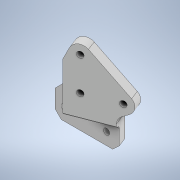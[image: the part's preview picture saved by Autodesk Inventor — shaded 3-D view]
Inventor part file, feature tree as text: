
AUTODESK INVENTOR PART (.ipt)
format: ipt  version: 2023 (Build 270158000, 158)  size: 296,448 bytes
history: native  units: mm
features: reference x11, extrude x9, sketch x9, projected_geometry x8, other x7, fillet x6, chamfer x4, thicken_offset x2
ambient origin geometry x8: Origin, YZ Plane, XZ Plane, XY Plane, X Axis, Y Axis, Z Axis, Center Point
bodies: Solid1 (feature_tree)
feature tree (56):
  extrude  "Extrusion1"  Depth=20.0mm
  extrude  "Extrusion2"  Depth=2.0mm
  extrude  "Extrusion3"  Depth=3.0mm TaperAngle=0.0deg
  extrude  "Extrusion4"  Depth=3.0mm TaperAngle=0.0deg
  extrude  "Extrusion5"  Depth=6.0mm
  extrude  "Extrusion6"  Depth=3.0mm
  extrude  "Extrusion7"  Depth=3.0mm TaperAngle=0.0deg
  fillet  "Fillet1"  Radius=6.0mm
  fillet  "Fillet2"  Radius=120.0mm
  chamfer  "Chamfer1"  Distance=3.0mm Angle=45.0deg
  extrude  "Extrusion8"  Depth=2.0mm
  extrude  "Extrusion9"  Depth=2.0mm
  chamfer  "Chamfer3"  Distance=2.0mm
  chamfer  "Chamfer4"  Distance=120.0mm
  thicken_offset  "Thicken1"
  thicken_offset  "Thicken2"
  fillet  "Fillet6"  Radius=120.0mm
  fillet  "Fillet7"  Radius=2.0mm
  fillet  "Fillet8"  Radius=2.0mm
  chamfer  "Chamfer5"  Distance=2.0mm
  fillet  "Fillet10"  Radius=1.5mm
  sketch  "Sketch1"  dims[d0=8.0mm d1=20.0mm]
  reference  "Reference1"
  reference  "Reference2"
  reference  "Reference3"
  sketch  "Sketch2"  dims[d2=2.0mm d3=2.0mm]
  projected_geometry  "Projected Loop1"
  reference  "Reference4"
  sketch  "Sketch3"  dims[d4=3.0mm d5=0.0mm d6=20.0mm d7=0.0mm]
  projected_geometry  "Projected Loop2"
  projected_geometry  "Projected Loop3"
  sketch  "Sketch4"  dims[d8=3.0mm d9=0.0mm d10=3.0mm d11=0.0mm]
  projected_geometry  "Projected Loop4"
  sketch  "Sketch5"  dims[d12=6.0mm d13=6.0mm]
  reference  "Reference5"
  reference  "Reference6"
  projected_geometry  "Projected Loop5"
  sketch  "Sketch6"  dims[d14=3.0mm d15=0.0mm d16=6.0mm]
  reference  "Reference7"
  reference  "Reference8"
  projected_geometry  "Projected Loop6"
  sketch  "Sketch7"  dims[d17=6.0mm d18=3.0mm d19=0.0mm d20=6.0mm d21=120.0mm d22=0.0mm]
  projected_geometry  "Projected Loop7"
  sketch  "Sketch8"  dims[d23=3.0mm]
  reference  "Reference9"
  reference  "Reference10"
  reference  "Reference11"
  sketch  "Sketch9"  dims[d24=1.0mm d25=3.0mm d26=2.0mm d27=45.0deg d28=2.0mm d29=2.0mm d30=2.0mm d31=120.0mm d32=0.0mm d33=120.0mm d34=0.0mm d41=2.0mm d42=2.0mm d43=45.0deg d44=2.0mm d45=2.0mm d46=45.0deg d47=2.0mm d48=1.0mm d49=1.5mm d50=1.5mm d51=2.0mm d52=3.0mm d53=1.5mm d54=0.5mm d55=2.0mm d56=45.0deg d58=2.0mm]
  projected_geometry  "Projected Loop8"
  parser-record x1  (decoder bookkeeping rows leaked as tree rows — omitted from the tree; the rows remain in map.json)
  other  "leg_1.iam"
  other  "leg_holder_2:1"
  other  "wh_ass_3:3"
  other  "screw_holder_2_3:2"
  other  "screw_holder_2_3:5"
  other  "tendon_wh_3:1"
note: 1 file-system path scrubbed to <path> (originals preserved in map.json)
